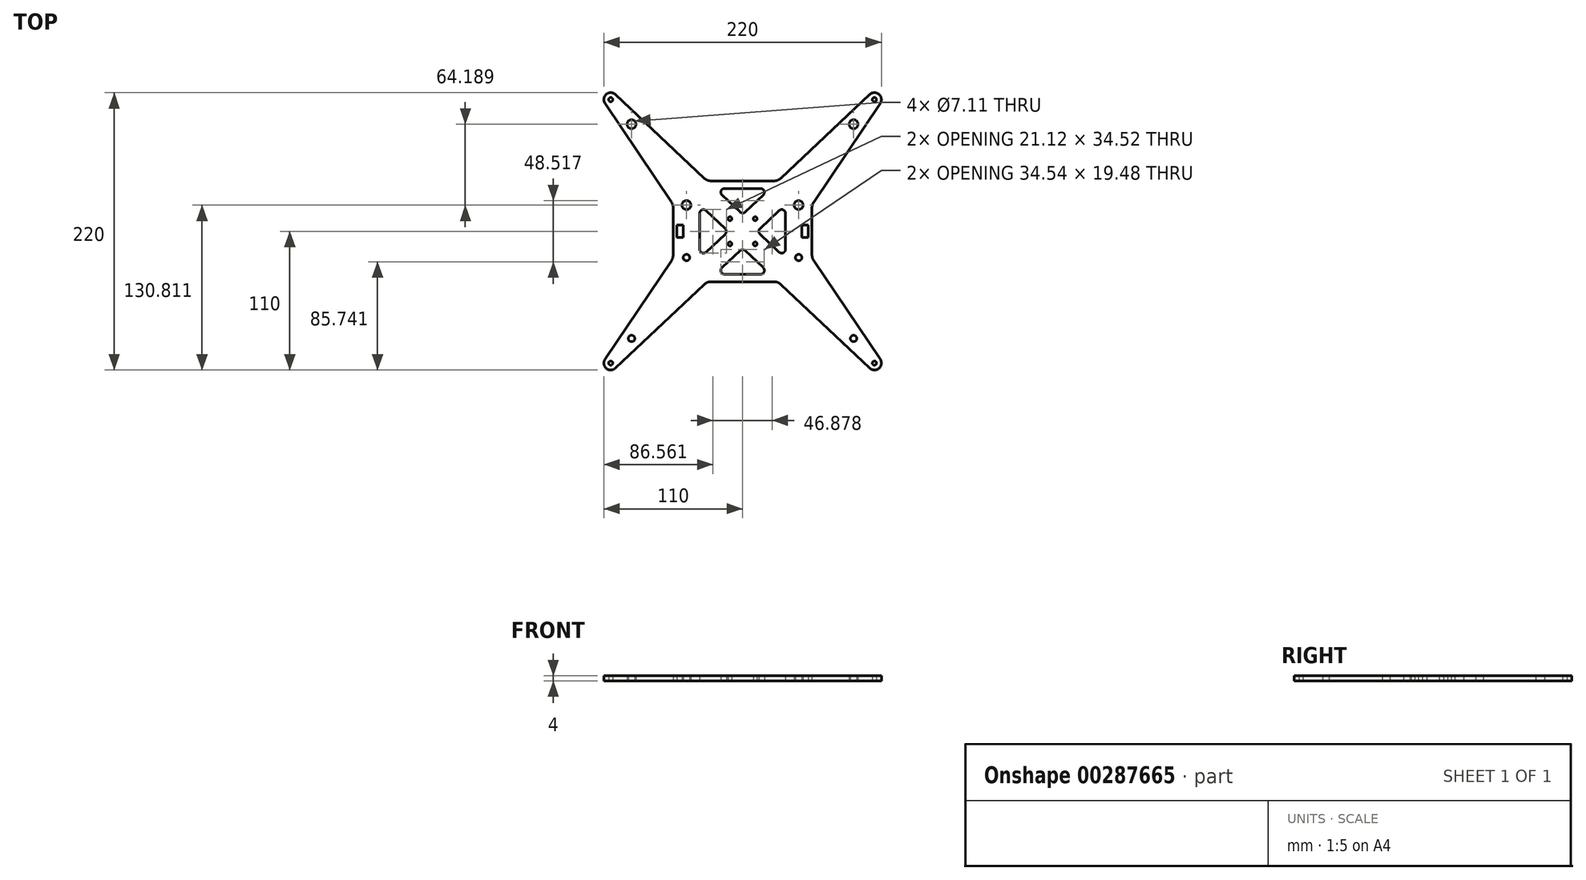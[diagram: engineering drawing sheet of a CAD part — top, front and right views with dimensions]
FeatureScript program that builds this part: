
annotation { "Feature Type Name" : "Feature", "Feature Type Description" : "" }
export const myFeature = defineFeature(function(context is Context, id is Id, definition is map)
    precondition{}
    {
        {
            var Q0;
            Q0=qCreatedBy(makeId("Top.planeOp"),FACE);
            var sketch = newSketch(context, id + "F0", { "sketchPlane" : qUnion([Q0])});
            skLineSegment(sketch, "E0", {"start": v(-28.94, 16.46) * mm, "end": v(-13.82, 2.18) * mm});
            skLineSegment(sketch, "E1", {"start": v(-13.82, -2.18) * mm, "end": v(-28.94, -16.46) * mm});
            skLineSegment(sketch, "E2", {"start": v(-34, -14.28) * mm, "end": v(-34, 14.28) * mm});
            skLineSegment(sketch, "E3", {"start": v(34, 14.28) * mm, "end": v(34, -14.28) * mm});
            skLineSegment(sketch, "E4", {"start": v(28.94, -16.46) * mm, "end": v(13.82, -2.18) * mm});
            skLineSegment(sketch, "E5", {"start": v(13.82, 2.18) * mm, "end": v(28.94, 16.46) * mm});
            skLineSegment(sketch, "E6", {"start": v(-16.34, -28.82) * mm, "end": v(-2.06, -15.34) * mm});
            skLineSegment(sketch, "E7", {"start": v(2.06, -15.34) * mm, "end": v(16.34, -28.82) * mm});
            skLineSegment(sketch, "E8", {"start": v(14.28, -34) * mm, "end": v(-14.28, -34) * mm});
            skLineSegment(sketch, "E9", {"start": v(16.34, 28.82) * mm, "end": v(2.06, 15.34) * mm});
            skLineSegment(sketch, "E10", {"start": v(-2.06, 15.34) * mm, "end": v(-16.34, 28.82) * mm});
            skLineSegment(sketch, "E11", {"start": v(-14.28, 34) * mm, "end": v(14.28, 34) * mm});
            skLineSegment(sketch, "E12", {"start": v(-47, -5) * mm, "end": v(-52, -5) * mm});
            skLineSegment(sketch, "E13", {"start": v(-52, -5) * mm, "end": v(-52, 5) * mm});
            skLineSegment(sketch, "E14", {"start": v(-52, 5) * mm, "end": v(-47, 5) * mm});
            skLineSegment(sketch, "E15", {"start": v(-47, 5) * mm, "end": v(-47, -5) * mm});
            skLineSegment(sketch, "E16", {"start": v(47, 5) * mm, "end": v(52, 5) * mm});
            skLineSegment(sketch, "E17", {"start": v(52, 5) * mm, "end": v(52, -5) * mm});
            skLineSegment(sketch, "E18", {"start": v(52, -5) * mm, "end": v(47, -5) * mm});
            skLineSegment(sketch, "E19", {"start": v(47, -5) * mm, "end": v(47, 5) * mm});
            skLineSegment(sketch, "E20", {"start": v(-55, 18.66) * mm, "end": v(-55, -18.66) * mm});
            skLineSegment(sketch, "E21", {"start": v(-56.36, -23.13) * mm, "end": v(-109.06, -101.43) * mm});
            skLineSegment(sketch, "E22", {"start": v(-100.72, -108.5) * mm, "end": v(-30.5, -42.18) * mm});
            skLineSegment(sketch, "E23", {"start": v(-25, -40) * mm, "end": v(25, -40) * mm});
            skLineSegment(sketch, "E24", {"start": v(30.5, -42.18) * mm, "end": v(100.72, -108.5) * mm});
            skLineSegment(sketch, "E25", {"start": v(109.06, -101.43) * mm, "end": v(56.36, -23.13) * mm});
            skLineSegment(sketch, "E26", {"start": v(55, -18.66) * mm, "end": v(55, 18.66) * mm});
            skLineSegment(sketch, "E27", {"start": v(56.36, 23.13) * mm, "end": v(109.06, 101.43) * mm});
            skLineSegment(sketch, "E28", {"start": v(100.72, 108.5) * mm, "end": v(30.5, 42.18) * mm});
            skLineSegment(sketch, "E29", {"start": v(25, 40) * mm, "end": v(-25, 40) * mm});
            skLineSegment(sketch, "E30", {"start": v(-30.5, 42.18) * mm, "end": v(-100.72, 108.5) * mm});
            skLineSegment(sketch, "E31", {"start": v(-109.06, 101.43) * mm, "end": v(-56.36, 23.13) * mm});
            skCircle(sketch, "E32", {"center": v(-87.97, 85) * mm, "radius": 3.56 * mm});
            skCircle(sketch, "E33", {"center": v(87.97, 85) * mm, "radius": 3.56 * mm});
            skCircle(sketch, "E34", {"center": v(-44.44, 20.81) * mm, "radius": 3.56 * mm});
            skCircle(sketch, "E35", {"center": v(44.44, 20.81) * mm, "radius": 3.56 * mm});
            skCircle(sketch, "E36", {"center": v(-87.97, -85) * mm, "radius": 2.55 * mm});
            skCircle(sketch, "E37", {"center": v(87.97, -85) * mm, "radius": 2.55 * mm});
            skCircle(sketch, "E38", {"center": v(-44.44, -20.8) * mm, "radius": 2.55 * mm});
            skCircle(sketch, "E39", {"center": v(44.44, -20.8) * mm, "radius": 2.55 * mm});
            skCircle(sketch, "E40", {"center": v(104.5, -104.5) * mm, "radius": 1.65 * mm});
            skCircle(sketch, "E41", {"center": v(-104.5, -104.5) * mm, "radius": 1.65 * mm});
            skCircle(sketch, "E42", {"center": v(104.5, 104.5) * mm, "radius": 1.65 * mm});
            skCircle(sketch, "E43", {"center": v(-104.5, 104.5) * mm, "radius": 1.65 * mm});
            skCircle(sketch, "E44", {"center": v(10, 10) * mm, "radius": 1.52 * mm});
            skCircle(sketch, "E45", {"center": v(10, -10) * mm, "radius": 1.52 * mm});
            skCircle(sketch, "E46", {"center": v(-10, -10) * mm, "radius": 1.52 * mm});
            skCircle(sketch, "E47", {"center": v(-10, 10) * mm, "radius": 1.52 * mm});
            skArc(sketch, "E48", {"start": v(-109.06, -101.43) * mm, "mid": v(-108.06, -108.7) * mm, "end": v(-100.72, -108.5) * mm});
            skArc(sketch, "E49", {"start": v(-100.72, 108.5) * mm, "mid": v(-108.06, 108.7) * mm, "end": v(-109.06, 101.43) * mm});
            skArc(sketch, "E50", {"start": v(109.06, 101.43) * mm, "mid": v(108.06, 108.7) * mm, "end": v(100.72, 108.5) * mm});
            skArc(sketch, "E51", {"start": v(100.72, -108.5) * mm, "mid": v(108.06, -108.7) * mm, "end": v(109.06, -101.43) * mm});
            skArc(sketch, "E52", {"start": v(-14.28, -34) * mm, "mid": v(-17.07, -32.1) * mm, "end": v(-16.34, -28.82) * mm});
            skArc(sketch, "E53", {"start": v(14.28, -34) * mm, "mid": v(17.07, -32.1) * mm, "end": v(16.34, -28.82) * mm});
            skArc(sketch, "E54", {"start": v(-2.06, -15.34) * mm, "mid": v(0, -14.52) * mm, "end": v(2.06, -15.34) * mm});
            skArc(sketch, "E55", {"start": v(13.82, 2.18) * mm, "mid": v(12.88, 0) * mm, "end": v(13.82, -2.18) * mm});
            skArc(sketch, "E56", {"start": v(28.94, -16.46) * mm, "mid": v(32.19, -17.03) * mm, "end": v(34, -14.28) * mm});
            skArc(sketch, "E57", {"start": v(28.94, 16.46) * mm, "mid": v(32.19, 17.03) * mm, "end": v(34, 14.28) * mm});
            skArc(sketch, "E58", {"start": v(-30.5, 42.18) * mm, "mid": v(-27.96, 40.57) * mm, "end": v(-25, 40) * mm});
            skArc(sketch, "E59", {"start": v(25, 40) * mm, "mid": v(27.96, 40.57) * mm, "end": v(30.5, 42.18) * mm});
            skArc(sketch, "E60", {"start": v(14.28, 34) * mm, "mid": v(17.07, 32.1) * mm, "end": v(16.34, 28.82) * mm});
            skArc(sketch, "E61", {"start": v(-14.28, 34) * mm, "mid": v(-17.07, 32.1) * mm, "end": v(-16.34, 28.82) * mm});
            skArc(sketch, "E62", {"start": v(-2.06, 15.34) * mm, "mid": v(0, 14.52) * mm, "end": v(2.06, 15.34) * mm});
            skArc(sketch, "E63", {"start": v(-56.36, 23.13) * mm, "mid": v(-55.35, 21) * mm, "end": v(-55, 18.66) * mm});
            skArc(sketch, "E64", {"start": v(-56.36, -23.13) * mm, "mid": v(-55.35, -21) * mm, "end": v(-55, -18.66) * mm});
            skArc(sketch, "E65", {"start": v(-34, 14.28) * mm, "mid": v(-32.19, 17.03) * mm, "end": v(-28.94, 16.46) * mm});
            skArc(sketch, "E66", {"start": v(-34, -14.28) * mm, "mid": v(-32.19, -17.03) * mm, "end": v(-28.94, -16.46) * mm});
            skArc(sketch, "E67", {"start": v(-13.82, 2.18) * mm, "mid": v(-12.88, 0) * mm, "end": v(-13.82, -2.18) * mm});
            skArc(sketch, "E68", {"start": v(-30.5, -42.18) * mm, "mid": v(-27.96, -40.57) * mm, "end": v(-25, -40) * mm});
            skArc(sketch, "E69", {"start": v(25, -40) * mm, "mid": v(27.96, -40.57) * mm, "end": v(30.5, -42.18) * mm});
            skArc(sketch, "E70", {"start": v(55, -18.66) * mm, "mid": v(55.35, -21) * mm, "end": v(56.36, -23.13) * mm});
            skArc(sketch, "E71", {"start": v(55, 18.66) * mm, "mid": v(55.35, 21) * mm, "end": v(56.36, 23.13) * mm});
            skSolve(sketch);
        }
        {
            var Q0;
            Q0=makeQuery(id+"F0.imprint","IMPRINT",FACE,{"disambiguationData":[TD([[makeQuery(id+"F0.imprint","IMPRINT",EDGE,{"derivedFrom":sQuery(id+"F0.wireOp",EDGE,"E0")}),1.0]])]});
            extrude(context, id + "F1", {"entities" : qUnion([Q0]), "depth" : 4 * mm, "offsetDistance" : 25 * mm});
        }
    });
